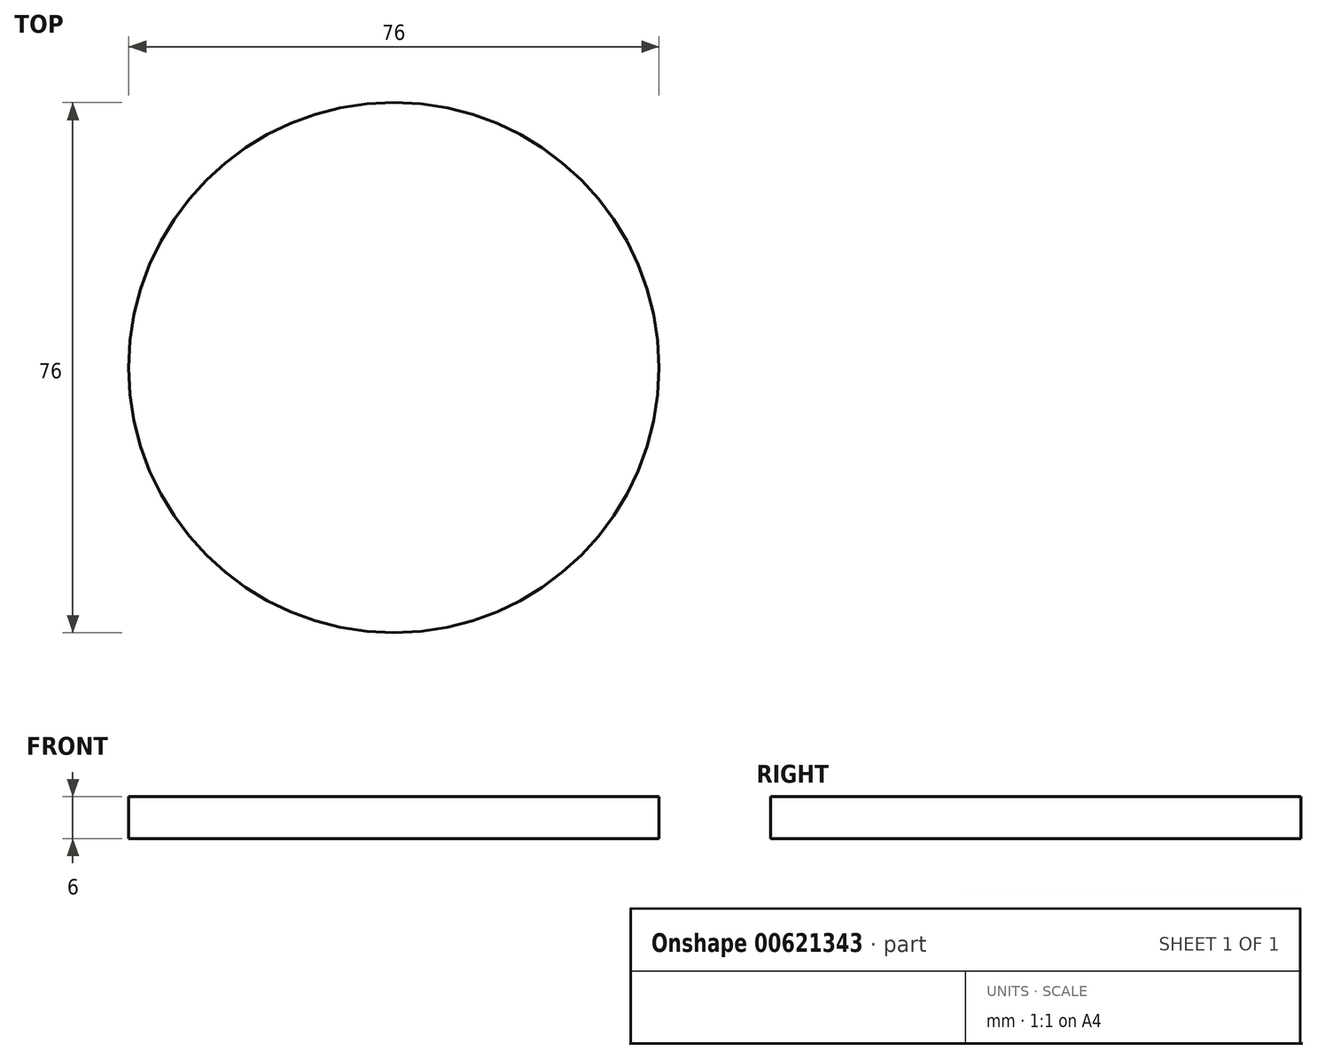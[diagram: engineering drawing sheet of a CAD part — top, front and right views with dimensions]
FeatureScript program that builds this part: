
annotation { "Feature Type Name" : "Feature", "Feature Type Description" : "" }
export const myFeature = defineFeature(function(context is Context, id is Id, definition is map)
    precondition{}
    {
        {
            var Q0;
            Q0=qCreatedBy(makeId("Top.planeOp"),FACE);
            var sketch = newSketch(context, id + "F0", { "sketchPlane" : qUnion([Q0])});
            skCircle(sketch, "E0", {"center": v(0, 0) * mm, "radius": 38 * mm});
            skSolve(sketch);
        }
        {
            var Q0;
            Q0 = qSketchRegion(id + "F0", true);
            extrude(context, id + "F1", {"entities" : qUnion([Q0]), "depth" : 6 * mm, "offsetDistance" : 25.4 * mm});
        }
    });
